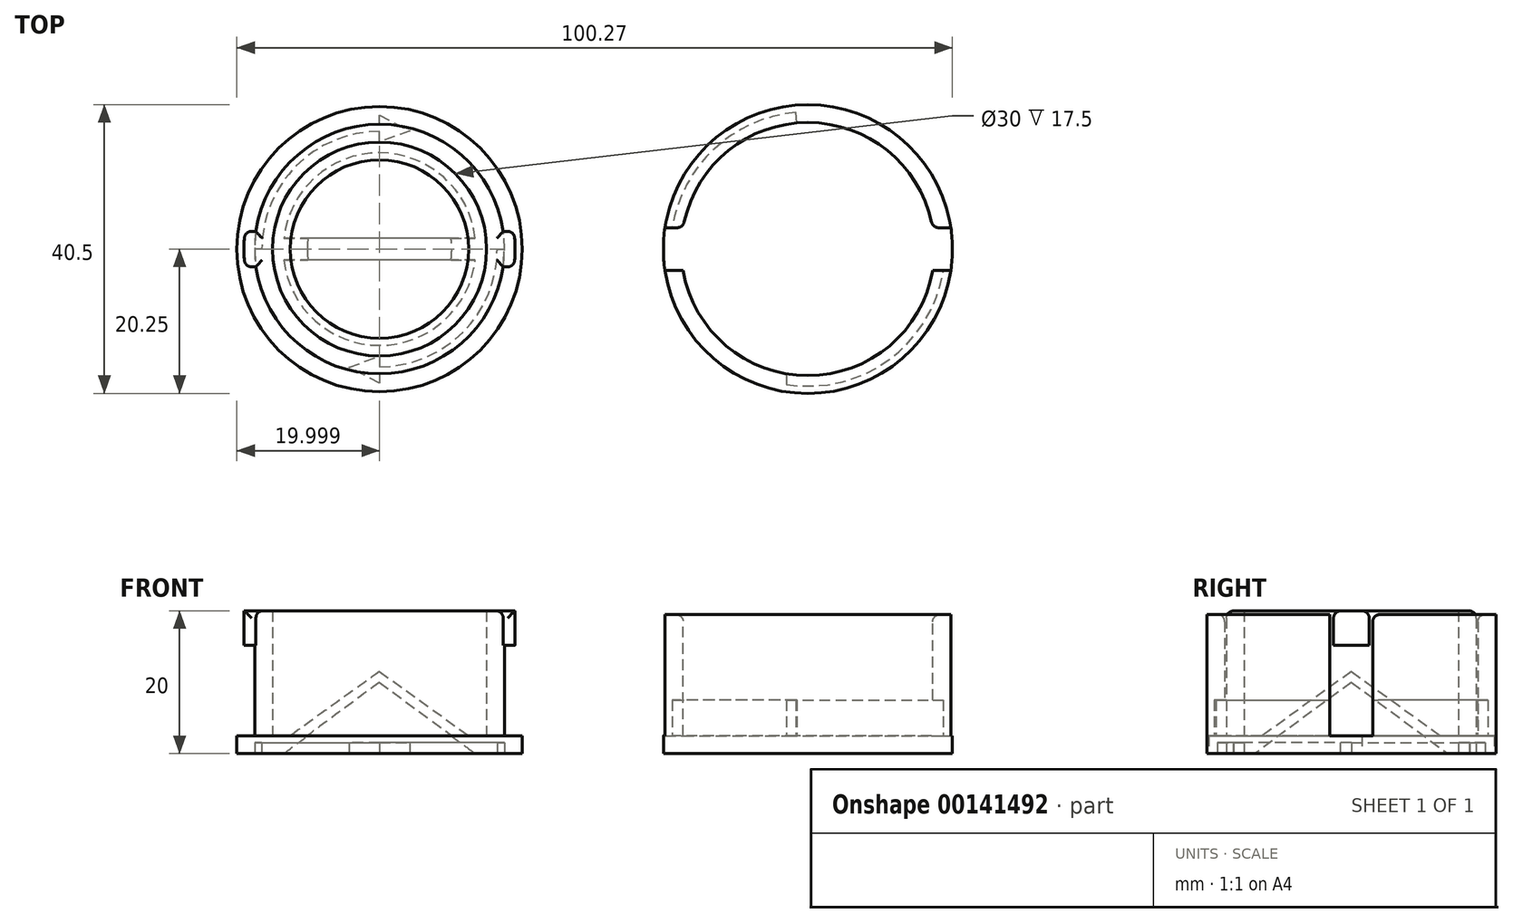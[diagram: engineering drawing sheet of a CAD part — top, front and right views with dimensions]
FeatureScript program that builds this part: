
annotation { "Feature Type Name" : "Feature", "Feature Type Description" : "" }
export const myFeature = defineFeature(function(context is Context, id is Id, definition is map)
    precondition{}
    {
        {
            var Q0;
            Q0=qCreatedBy(makeId("Top.planeOp"),FACE);
            var sketch = newSketch(context, id + "F0", { "sketchPlane" : qUnion([Q0])});
            skCircle(sketch, "E0", {"center": v(-83.34, 0) * mm, "radius": 20.25 * mm});
            skSolve(sketch);
        }
        {
            var Q0;
            Q0=makeQuery(id+"F0.imprint","IMPRINT",FACE,{"disambiguationData":[TD([[makeQuery(id+"F0.imprint","IMPRINT",EDGE,{"derivedFrom":sQuery(id+"F0.wireOp",EDGE,"E0")}),1.0]])]});
            extrude(context, id + "F1", {"entities" : qUnion([Q0]), "depth" : (22 - 2.5) * mm});
        }
        {
            var Q0;
            Q0=makeQuery(id+"F1.opExtrude","CAP_FACE",FACE,{"disambiguationData":[OSD([sQuery(id+"F0.wireOp",EDGE,"E0")])],"isStart":false});
            shell(context, id + "F2", {"entities" : qUnion([Q0]), "thickness" : 2.5 * mm});
        }
        {
            var Q0;
            Q0=makeQuery(id+"F1.opExtrude","CAP_FACE",FACE,{"disambiguationData":[OSD([sQuery(id+"F0.wireOp",EDGE,"E0")])],"isStart":false});
            var sketch = newSketch(context, id + "F3", { "sketchPlane" : qUnion([Q0])});
            skLineSegment(sketch, "E1.bottom", {"start": v(-105.34, -3) * mm, "end": v(-61.34, -3) * mm});
            skLineSegment(sketch, "E1.top", {"start": v(-105.34, 3) * mm, "end": v(-61.34, 3) * mm});
            skLineSegment(sketch, "E1.left", {"start": v(-105.34, -3) * mm, "end": v(-105.34, 3) * mm});
            skLineSegment(sketch, "E1.right", {"start": v(-61.34, -3) * mm, "end": v(-61.34, 3) * mm});
            skPoint(sketch, "E1.middle", {"position": v(-83.34, 0) * mm});
            skSolve(sketch);
        }
        {
            var Q0;
            {var subQ0=sQuery(id+"F3.wireOp",EDGE,"E1.bottom");var subQ1=sQuery(id+"F0.wireOp",EDGE,"E0");var subQ2=makeQuery(id+"F1.opExtrude","CAP_EDGE",EDGE,{"disambiguationData":[OSD([subQ1])],"isStart":false});var subQ3=makeQuery(id+"F3.imprint","INTERSECT",VERTEX,{"disambiguationData":[OD(1.0)],"derivedFrom":[subQ2,subQ0]});Q0=makeQuery(id+"F3.imprint","IMPRINT",FACE,{"disambiguationData":[TD([[makeQuery(id+"F3.imprint","IMPRINT",EDGE,{"disambiguationData":[TD([[subQ3,-1.0]])],"derivedFrom":subQ2}),1.0]])]});}
            var Q1;
            {var subQ0=sQuery(id+"F3.wireOp",EDGE,"E1.bottom");var subQ1=sQuery(id+"F0.wireOp",EDGE,"E0");var subQ2=makeQuery(id+"F1.opExtrude","CAP_EDGE",EDGE,{"disambiguationData":[OSD([subQ1])],"isStart":false});var subQ3=makeQuery(id+"F3.imprint","INTERSECT",VERTEX,{"disambiguationData":[OD(0.0)],"derivedFrom":[subQ2,subQ0]});Q1=makeQuery(id+"F3.imprint","IMPRINT",FACE,{"disambiguationData":[TD([[makeQuery(id+"F3.imprint","IMPRINT",EDGE,{"disambiguationData":[TD([[subQ3,1.0]])],"derivedFrom":subQ2}),1.0]])]});}
            extrude(context, id + "F4", {"entities" : qUnion([Q0, Q1]), "operationType" : NewBodyOperationType.REMOVE, "oppositeDirection" : true, "depth" : (19.5 - 2.5) * mm});
        }
        {
            var Q0;
            {var subQ0=sQuery(id+"F3.wireOp",EDGE,"E1.bottom");var subQ1=sQuery(id+"F0.wireOp",EDGE,"E0");var subQ2=makeQuery(id+"F1.opExtrude","CAP_EDGE",EDGE,{"disambiguationData":[OSD([subQ1])],"isStart":false});var subQ3=makeQuery(id+"F2.opShell","OFFSET_EDGE",EDGE,{"disambiguationData":[OSD([subQ1]),TDD([subQ2])]});var subQ4=makeQuery(id+"F3.imprint","INTERSECT",VERTEX,{"disambiguationData":[OD(1.0)],"derivedFrom":[subQ3,subQ0]});var subQ5=sQuery(id+"F3.wireOp",EDGE,"E1.top");var subQ7=makeQuery(id+"F3.imprint","INTERSECT",VERTEX,{"disambiguationData":[OD(1.0)],"derivedFrom":[subQ2,subQ0]});var subQ8=makeQuery(id+"F3.imprint","INTERSECT",VERTEX,{"disambiguationData":[OD(1.0)],"derivedFrom":[subQ2,subQ5]});var subQ9=makeQuery(id+"F3.imprint","INTERSECT",VERTEX,{"disambiguationData":[OD(0.0)],"derivedFrom":[subQ3,subQ0]});var subQ11=makeQuery(id+"F3.imprint","INTERSECT",VERTEX,{"disambiguationData":[OD(0.0)],"derivedFrom":[subQ2,subQ0]});var subQ12=makeQuery(id+"F3.imprint","INTERSECT",VERTEX,{"disambiguationData":[OD(0.0)],"derivedFrom":[subQ2,subQ5]});Q0=makeQuery(id+"F4.boolean.opBoolean","MERGE",FACE,{"derivedFrom":[makeQuery(id+"F2.opShell","OFFSET_FACE",FACE,{"disambiguationData":[OSD([subQ1]),TDD([makeQuery(id+"F1.opExtrude","CAP_FACE",FACE,{"disambiguationData":[OSD([subQ1])],"isStart":true})])]}),makeQuery(id+"F4.opExtrude","CAP_FACE",FACE,{"disambiguationData":[OSD([subQ1,subQ0,subQ5]),TDD([makeQuery(id+"F3.imprint","IMPRINT",EDGE,{"disambiguationData":[TD([[subQ11,-1.0]])],"derivedFrom":subQ0}),makeQuery(id+"F3.imprint","IMPRINT",EDGE,{"disambiguationData":[TD([[subQ12,-1.0]])],"derivedFrom":subQ5}),makeQuery(id+"F3.imprint","IMPRINT",EDGE,{"disambiguationData":[TD([[subQ11,1.0]])],"derivedFrom":subQ2}),makeQuery(id+"F3.imprint","IMPRINT",EDGE,{"disambiguationData":[TD([[subQ9,1.0]])],"derivedFrom":subQ3})])],"isStart":false}),makeQuery(id+"F4.opExtrude","CAP_FACE",FACE,{"disambiguationData":[OSD([subQ1,subQ0,subQ5]),TDD([makeQuery(id+"F3.imprint","IMPRINT",EDGE,{"disambiguationData":[TD([[subQ7,1.0]])],"derivedFrom":subQ0}),makeQuery(id+"F3.imprint","IMPRINT",EDGE,{"disambiguationData":[TD([[subQ8,1.0]])],"derivedFrom":subQ5}),makeQuery(id+"F3.imprint","IMPRINT",EDGE,{"disambiguationData":[TD([[subQ7,-1.0]])],"derivedFrom":subQ2}),makeQuery(id+"F3.imprint","IMPRINT",EDGE,{"disambiguationData":[TD([[subQ4,-1.0]])],"derivedFrom":subQ3})])],"isStart":false})]});}
            var sketch = newSketch(context, id + "F5", { "sketchPlane" : qUnion([Q0])});
            skLineSegment(sketch, "E2.0.1", {"start": v(-102.33, 3) * mm, "end": v(-100.83, 3) * mm});
            skArc(sketch, "E2.0.2", {"start": v(-100.83, 3) * mm, "mid": v(-95.37, 13.05) * mm, "end": v(-84.9, 17.68) * mm});
            skLineSegment(sketch, "E3.0.2", {"start": v(-64.34, -3) * mm, "end": v(-65.84, -3) * mm});
            skArc(sketch, "E3.0.3", {"start": v(-65.84, -3) * mm, "mid": v(-73.09, -14.5) * mm, "end": v(-86.34, -17.5) * mm});
            skLineSegment(sketch, "E4", {"start": v(-86.34, -17.5) * mm, "end": v(-86.34, -19) * mm});
            skPoint(sketch, "E4.endSnap0", {"position": v(-86.34, -20.16) * mm});
            skPoint(sketch, "E2.0.3.end.orphan", {"position": v(-63.3, 3) * mm});
            skPoint(sketch, "E2.0.3.start.orphan", {"position": v(-65.84, 3) * mm});
            skPoint(sketch, "E3.0.0.end.orphan", {"position": v(-103.36, -3) * mm});
            skPoint(sketch, "E3.0.0.start.orphan", {"position": v(-100.83, -3) * mm});
            skPoint(sketch, "E5.orphan", {"position": v(-86.34, -22.28) * mm});
            skArc(sketch, "E6.0", {"start": v(-86.34, -19) * mm, "mid": v(-72.03, -15.55) * mm, "end": v(-64.34, -3) * mm});
            skArc(sketch, "E7.0", {"start": v(-85.03, 19.16) * mm, "mid": v(-96.46, 14.05) * mm, "end": v(-102.33, 3) * mm});
            skPoint(sketch, "E8.orphan", {"position": v(-63.3, -3) * mm});
            skPoint(sketch, "E2.0.0.end.orphan", {"position": v(-103.36, 3) * mm});
            skLineSegment(sketch, "E9", {"start": v(-84.9, 17.68) * mm, "end": v(-85.03, 19.16) * mm});
            skSolve(sketch);
        }
        {
            var Q0;
            Q0 = qSketchRegion(id + "F5", true);
            extrude(context, id + "F6", {"entities" : qUnion([Q0]), "depth" : 5 * mm});
        }
        {
            var Q0;
            Q0=makeQuery(id+"F6.opExtrude","SWEPT_BODY",BODY,{"disambiguationData":[OSD([sQuery(id+"F5.wireOp",EDGE,"E2.0.0"),sQuery(id+"F5.wireOp",EDGE,"E2.0.1"),sQuery(id+"F5.wireOp",EDGE,"E2.0.2"),sQuery(id+"F5.wireOp",EDGE,"b0c8b627-6731-4ba6-8ec9-004736f8713d.trimOffspring")])]});
            var Q1;
            Q1=makeQuery(id+"F6.opExtrude","SWEPT_BODY",BODY,{"disambiguationData":[OSD([sQuery(id+"F5.wireOp",EDGE,"E3.0.1"),sQuery(id+"F5.wireOp",EDGE,"E3.0.2"),sQuery(id+"F5.wireOp",EDGE,"E3.0.3"),sQuery(id+"F5.wireOp",EDGE,"E4")])]});
            var Q2;
            Q2=makeQuery(id+"F1.opExtrude","SWEPT_BODY",BODY,{"disambiguationData":[OSD([sQuery(id+"F0.wireOp",EDGE,"E0")])]});
            booleanBodies(context, id + "F7", {"operationType" : BooleanOperationType.SUBTRACTION, "tools" : qUnion([Q0, Q1]), "targets" : qUnion([Q2])});
        }
        {
            var Q0;
            {var subQ0=sQuery(id+"F3.wireOp",EDGE,"E1.bottom");var subQ1=sQuery(id+"F0.wireOp",EDGE,"E0");var subQ2=makeQuery(id+"F1.opExtrude","CAP_EDGE",EDGE,{"disambiguationData":[OSD([subQ1])],"isStart":false});Q0=makeQuery(id+"F4.boolean.opBoolean","COPY",EDGE,{"derivedFrom":makeQuery(id+"F4.opExtrude","CAP_EDGE",EDGE,{"disambiguationData":[OSD([subQ0]),TDD([makeQuery(id+"F3.imprint","IMPRINT",EDGE,{"disambiguationData":[TD([[makeQuery(id+"F3.imprint","INTERSECT",VERTEX,{"disambiguationData":[OD(1.0)],"derivedFrom":[subQ2,subQ0]}),1.0]])],"derivedFrom":subQ0})])],"isStart":true})});}
            var Q1;
            {var subQ0=sQuery(id+"F3.wireOp",EDGE,"E1.top");var subQ1=sQuery(id+"F0.wireOp",EDGE,"E0");var subQ2=makeQuery(id+"F1.opExtrude","CAP_EDGE",EDGE,{"disambiguationData":[OSD([subQ1])],"isStart":false});Q1=makeQuery(id+"F4.boolean.opBoolean","COPY",EDGE,{"derivedFrom":makeQuery(id+"F4.opExtrude","CAP_EDGE",EDGE,{"disambiguationData":[OSD([subQ0]),TDD([makeQuery(id+"F3.imprint","IMPRINT",EDGE,{"disambiguationData":[TD([[makeQuery(id+"F3.imprint","INTERSECT",VERTEX,{"disambiguationData":[OD(1.0)],"derivedFrom":[subQ2,subQ0]}),1.0]])],"derivedFrom":subQ0})])],"isStart":true})});}
            var Q2;
            {var subQ0=sQuery(id+"F3.wireOp",EDGE,"E1.top");var subQ1=sQuery(id+"F0.wireOp",EDGE,"E0");var subQ2=makeQuery(id+"F1.opExtrude","CAP_EDGE",EDGE,{"disambiguationData":[OSD([subQ1])],"isStart":false});Q2=makeQuery(id+"F4.boolean.opBoolean","COPY",EDGE,{"derivedFrom":makeQuery(id+"F4.opExtrude","CAP_EDGE",EDGE,{"disambiguationData":[OSD([subQ0]),TDD([makeQuery(id+"F3.imprint","IMPRINT",EDGE,{"disambiguationData":[TD([[makeQuery(id+"F3.imprint","INTERSECT",VERTEX,{"disambiguationData":[OD(0.0)],"derivedFrom":[subQ2,subQ0]}),-1.0]])],"derivedFrom":subQ0})])],"isStart":true})});}
            var Q3;
            {var subQ0=sQuery(id+"F3.wireOp",EDGE,"E1.bottom");var subQ1=sQuery(id+"F0.wireOp",EDGE,"E0");var subQ2=makeQuery(id+"F1.opExtrude","CAP_EDGE",EDGE,{"disambiguationData":[OSD([subQ1])],"isStart":false});Q3=makeQuery(id+"F4.boolean.opBoolean","COPY",EDGE,{"derivedFrom":makeQuery(id+"F4.opExtrude","CAP_EDGE",EDGE,{"disambiguationData":[OSD([subQ0]),TDD([makeQuery(id+"F3.imprint","IMPRINT",EDGE,{"disambiguationData":[TD([[makeQuery(id+"F3.imprint","INTERSECT",VERTEX,{"disambiguationData":[OD(0.0)],"derivedFrom":[subQ2,subQ0]}),-1.0]])],"derivedFrom":subQ0})])],"isStart":true})});}
            var Q4;
            Q4=makeQuery(id+"F7.opBoolean","COPY",EDGE,{"derivedFrom":makeQuery(id+"F6.opExtrude","SWEPT_EDGE",EDGE,{"disambiguationData":[OSD([sQuery(id+"F3.wireOp",EDGE,"E1.bottom"),sQuery(id+"F5.wireOp",EDGE,"E3.0.2"),sQuery(id+"F5.wireOp",EDGE,"E6.0")])]})});
            var Q5;
            Q5=makeQuery(id+"F7.opBoolean","COPY",EDGE,{"derivedFrom":makeQuery(id+"F6.opExtrude","SWEPT_EDGE",EDGE,{"disambiguationData":[OSD([sQuery(id+"F3.wireOp",EDGE,"E1.top"),sQuery(id+"F5.wireOp",EDGE,"E2.0.1"),sQuery(id+"F5.wireOp",EDGE,"E7.0")])]})});
            fillet(context, id + "F8", {"entities" : qUnion([Q0, Q1, Q2, Q3, Q4, Q5]), "radius" : 1 * mm, "tangentPropagation" : true, "allowEdgeOverflow" : false});
        }
        {
            var Q0;
            {var subQ0=sQuery(id+"F0.wireOp",EDGE,"E0");var subQ1=sQuery(id+"F3.wireOp",EDGE,"E1.top");var subQ2=makeQuery(id+"F1.opExtrude","CAP_EDGE",EDGE,{"disambiguationData":[OSD([subQ0])],"isStart":false});var subQ3=makeQuery(id+"F2.opShell","OFFSET_EDGE",EDGE,{"disambiguationData":[OSD([subQ0]),TDD([subQ2])]});Q0=makeQuery(id+"F4.boolean.opBoolean","SPLIT",EDGE,{"disambiguationData":[TD([makeQuery(id+"F4.opExtrude","SWEPT_FACE",FACE,{"disambiguationData":[OSD([subQ1]),TDD([makeQuery(id+"F3.imprint","IMPRINT",EDGE,{"disambiguationData":[TD([[makeQuery(id+"F3.imprint","INTERSECT",VERTEX,{"disambiguationData":[OD(0.0)],"derivedFrom":[subQ2,subQ1]}),-1.0]])],"derivedFrom":subQ1})])]})])],"derivedFrom":subQ3});}
            var Q1;
            {var subQ0=sQuery(id+"F0.wireOp",EDGE,"E0");var subQ1=sQuery(id+"F3.wireOp",EDGE,"E1.bottom");var subQ2=makeQuery(id+"F1.opExtrude","CAP_EDGE",EDGE,{"disambiguationData":[OSD([subQ0])],"isStart":false});var subQ3=makeQuery(id+"F2.opShell","OFFSET_EDGE",EDGE,{"disambiguationData":[OSD([subQ0]),TDD([subQ2])]});Q1=makeQuery(id+"F4.boolean.opBoolean","SPLIT",EDGE,{"disambiguationData":[TD([makeQuery(id+"F4.opExtrude","SWEPT_FACE",FACE,{"disambiguationData":[OSD([subQ1]),TDD([makeQuery(id+"F3.imprint","IMPRINT",EDGE,{"disambiguationData":[TD([[makeQuery(id+"F3.imprint","INTERSECT",VERTEX,{"disambiguationData":[OD(0.0)],"derivedFrom":[subQ2,subQ1]}),-1.0]])],"derivedFrom":subQ1})])]})])],"derivedFrom":subQ3});}
            fillet(context, id + "F9", {"entities" : qUnion([Q0, Q1]), "radius" : 1 * mm, "tangentPropagation" : true, "allowEdgeOverflow" : false});
        }
        {
            var Q0;
            Q0=qCreatedBy(makeId("Front.planeOp"),FACE);
            var sketch = newSketch(context, id + "F10", { "sketchPlane" : qUnion([Q0])});
            skLineSegment(sketch, "E10", {"start": v(-123.36, 0) * mm, "end": v(-163.36, 0) * mm, "construction": true});
            skLineSegment(sketch, "E11", {"start": v(-123.36, 0) * mm, "end": v(-129.86, 0) * mm});
            skLineSegment(sketch, "E12", {"start": v(-129.86, 0) * mm, "end": v(-143.36, 10) * mm});
            skPoint(sketch, "E12.endSnap0", {"position": v(-143.36, 0) * mm});
            skLineSegment(sketch, "E13", {"start": v(-143.36, 10) * mm, "end": v(-143.36, 11.5) * mm});
            skLineSegment(sketch, "E14", {"start": v(-143.36, 11.5) * mm, "end": v(-130.86, 2.5) * mm});
            skLineSegment(sketch, "E15", {"start": v(-130.86, 2.5) * mm, "end": v(-128.36, 2.5) * mm});
            skLineSegment(sketch, "E16", {"start": v(-128.36, 2.5) * mm, "end": v(-128.36, 20) * mm});
            skLineSegment(sketch, "E17", {"start": v(-128.36, 20) * mm, "end": v(-125.86, 20) * mm});
            skLineSegment(sketch, "E18", {"start": v(-125.86, 20) * mm, "end": v(-125.86, 2.5) * mm});
            skLineSegment(sketch, "E19", {"start": v(-125.86, 2.5) * mm, "end": v(-123.36, 2.5) * mm});
            skLineSegment(sketch, "E20", {"start": v(-123.36, 2.5) * mm, "end": v(-123.36, 0) * mm});
            skSolve(sketch);
        }
        {
            var Q0;
            Q0=makeQuery(id+"F10.imprint","IMPRINT",FACE,{"disambiguationData":[TD([[makeQuery(id+"F10.imprint","IMPRINT",EDGE,{"derivedFrom":sQuery(id+"F10.wireOp",EDGE,"E11")}),-1.0]])]});
            var Q1;
            Q1=sQuery(id+"F10.wireOp",EDGE,"E13");
            revolve(context, id + "F11", {"entities" : qUnion([Q0]), "axis" : qUnion([Q1]), "revolveType" : RevolveType.FULL});
        }
        {
            var Q0;
            Q0=makeQuery(id+"F11.opRevolve","SWEPT_FACE",FACE,{"disambiguationData":[OSD([sQuery(id+"F10.wireOp",EDGE,"E11")])]});
            var sketch = newSketch(context, id + "F12", { "sketchPlane" : qUnion([Q0])});
            skCircle(sketch, "E21.0", {"center": v(-143.36, 0) * mm, "radius": 17.5 * mm, "construction": true});
            skCircle(sketch, "E22.0", {"center": v(-143.4, 0.19) * mm, "radius": 16.7 * mm, "construction": true});
            skLineSegment(sketch, "E23.bottom", {"start": v(-126.8, -1.5) * mm, "end": v(-159.93, -1.5) * mm});
            skLineSegment(sketch, "E23.top", {"start": v(-126.8, 1.5) * mm, "end": v(-159.93, 1.5) * mm});
            skLineSegment(sketch, "E23.left", {"start": v(-126.8, -1.5) * mm, "end": v(-126.8, 1.5) * mm});
            skLineSegment(sketch, "E23.right", {"start": v(-159.93, -1.5) * mm, "end": v(-159.93, 1.5) * mm});
            skSolve(sketch);
        }
        {
            var Q0;
            {var subQ0=sQuery(id+"F12.wireOp",EDGE,"E23.bottom");var subQ1=makeQuery(id+"F11.opRevolve","SWEPT_EDGE",EDGE,{"disambiguationData":[OSD([sQuery(id+"F10.wireOp",EDGE,"E11"),sQuery(id+"F10.wireOp",EDGE,"E12")])]});var subQ2=makeQuery(id+"F12.imprint","INTERSECT",VERTEX,{"disambiguationData":[OD(0.0)],"derivedFrom":[subQ1,subQ0]});Q0=makeQuery(id+"F12.imprint","IMPRINT",FACE,{"disambiguationData":[TD([[makeQuery(id+"F12.imprint","IMPRINT",EDGE,{"disambiguationData":[TD([[subQ2,-1.0]])],"derivedFrom":subQ0}),-1.0]])]});}
            extrude(context, id + "F13", {"entities" : qUnion([Q0]), "operationType" : NewBodyOperationType.ADD, "oppositeDirection" : true, "depth" : 2.5 * mm});
        }
        {
            var Q0;
            Q0=makeQuery(id+"F11.opRevolve","SWEPT_FACE",FACE,{"disambiguationData":[OSD([sQuery(id+"F10.wireOp",EDGE,"E17")])]});
            var sketch = newSketch(context, id + "F14", { "sketchPlane" : qUnion([Q0])});
            skCircle(sketch, "E24.0", {"center": v(-143.36, 0) * mm, "radius": 17.5 * mm});
            skLineSegment(sketch, "E25.bottom", {"start": v(-162.2, 2.5) * mm, "end": v(-160.68, 2.5) * mm});
            skLineSegment(sketch, "E25.top", {"start": v(-162.2, -2.5) * mm, "end": v(-160.68, -2.5) * mm});
            skArc(sketch, "E26.0", {"start": v(-124.53, -2.5) * mm, "mid": v(-124.36, 0) * mm, "end": v(-124.53, 2.5) * mm});
            skPoint(sketch, "E25.left.end.orphan", {"position": v(-165.72, -2.5) * mm});
            skPoint(sketch, "E27.orphan", {"position": v(-165.72, 2.5) * mm});
            skArc(sketch, "E28.trimOffspring", {"start": v(-162.2, 2.5) * mm, "mid": v(-162.36, 0) * mm, "end": v(-162.2, -2.5) * mm});
            skLineSegment(sketch, "E29.trimOffspring", {"start": v(-126.04, 2.5) * mm, "end": v(-124.53, 2.5) * mm});
            skLineSegment(sketch, "E30.trimOffspring", {"start": v(-126.04, -2.5) * mm, "end": v(-124.53, -2.5) * mm});
            skPoint(sketch, "E25.right.start.orphan", {"position": v(-121, 2.5) * mm});
            skPoint(sketch, "E31.orphan", {"position": v(-121, -2.5) * mm});
            skSolve(sketch);
        }
        {
            var Q0;
            Q0=makeQuery(id+"F14.imprint","IMPRINT",FACE,{"disambiguationData":[TD([[makeQuery(id+"F14.imprint","IMPRINT",EDGE,{"derivedFrom":sQuery(id+"F14.wireOp",EDGE,"E26.0")}),1.0]])]});
            var Q1;
            {var subQ0=sQuery(id+"F14.wireOp",EDGE,"E25.bottom");Q1=makeQuery(id+"F14.imprint","IMPRINT",FACE,{"disambiguationData":[TD([[makeQuery(id+"F14.imprint","IMPRINT",EDGE,{"derivedFrom":subQ0}),-1.0]])]});}
            extrude(context, id + "F15", {"entities" : qUnion([Q0, Q1]), "operationType" : NewBodyOperationType.ADD, "oppositeDirection" : true, "depth" : 4.8 * mm});
        }
        {
            var Q0;
            {var subQ0=sQuery(id+"F14.wireOp",EDGE,"E25.bottom");var subQ3=sQuery(id+"F10.wireOp",EDGE,"E18");var subQ4=sQuery(id+"F10.wireOp",EDGE,"E17");Q0=makeQuery(id+"F15.boolean.opBoolean","SPLIT",EDGE,{"disambiguationData":[TD([makeQuery(id+"F15.opExtrude","SWEPT_FACE",FACE,{"disambiguationData":[OSD([subQ0])]})])],"derivedFrom":makeQuery(id+"F11.opRevolve","SWEPT_EDGE",EDGE,{"disambiguationData":[OSD([subQ4,subQ3])]})});}
            var Q1;
            {var subQ0=sQuery(id+"F14.wireOp",EDGE,"E25.top");var subQ3=sQuery(id+"F10.wireOp",EDGE,"E18");var subQ4=sQuery(id+"F10.wireOp",EDGE,"E17");Q1=makeQuery(id+"F15.boolean.opBoolean","SPLIT",EDGE,{"disambiguationData":[TD([makeQuery(id+"F15.opExtrude","SWEPT_FACE",FACE,{"disambiguationData":[OSD([subQ0])]})])],"derivedFrom":makeQuery(id+"F11.opRevolve","SWEPT_EDGE",EDGE,{"disambiguationData":[OSD([subQ4,subQ3])]})});}
            var Q2;
            Q2=makeQuery(id+"F15.opExtrude","CAP_EDGE",EDGE,{"disambiguationData":[OSD([sQuery(id+"F14.wireOp",EDGE,"E29.trimOffspring")])],"isStart":true});
            var Q3;
            Q3=makeQuery(id+"F15.opExtrude","CAP_EDGE",EDGE,{"disambiguationData":[OSD([sQuery(id+"F14.wireOp",EDGE,"E30.trimOffspring")])],"isStart":true});
            var Q4;
            Q4=makeQuery(id+"F15.opExtrude","CAP_EDGE",EDGE,{"disambiguationData":[OSD([sQuery(id+"F14.wireOp",EDGE,"E25.bottom")])],"isStart":true});
            var Q5;
            Q5=makeQuery(id+"F15.opExtrude","CAP_EDGE",EDGE,{"disambiguationData":[OSD([sQuery(id+"F14.wireOp",EDGE,"E25.top")])],"isStart":true});
            var Q6;
            Q6=makeQuery(id+"F15.opExtrude","SWEPT_EDGE",EDGE,{"disambiguationData":[OSD([sQuery(id+"F14.wireOp",EDGE,"E25.bottom"),sQuery(id+"F14.wireOp",EDGE,"E28.trimOffspring")])]});
            var Q7;
            Q7=makeQuery(id+"F15.opExtrude","SWEPT_EDGE",EDGE,{"disambiguationData":[OSD([sQuery(id+"F14.wireOp",EDGE,"E25.top"),sQuery(id+"F14.wireOp",EDGE,"E28.trimOffspring")])]});
            var Q8;
            Q8=makeQuery(id+"F15.opExtrude","SWEPT_EDGE",EDGE,{"disambiguationData":[OSD([sQuery(id+"F14.wireOp",EDGE,"E26.0"),sQuery(id+"F14.wireOp",EDGE,"E30.trimOffspring")])]});
            var Q9;
            Q9=makeQuery(id+"F15.opExtrude","SWEPT_EDGE",EDGE,{"disambiguationData":[OSD([sQuery(id+"F14.wireOp",EDGE,"E26.0"),sQuery(id+"F14.wireOp",EDGE,"E29.trimOffspring")])]});
            fillet(context, id + "F16", {"entities" : qUnion([Q0, Q1, Q2, Q3, Q4, Q5, Q6, Q7, Q8, Q9]), "radius" : 1 * mm, "tangentPropagation" : true, "allowEdgeOverflow" : false});
        }
        {
            var Q0;
            {var subQ0=sQuery(id+"F10.wireOp",EDGE,"E11");Q0=makeQuery(id+"F13.boolean.opBoolean","MERGE",FACE,{"derivedFrom":[makeQuery(id+"F11.opRevolve","SWEPT_FACE",FACE,{"disambiguationData":[OSD([subQ0])]}),makeQuery(id+"F13.opExtrude","CAP_FACE",FACE,{"disambiguationData":[OSD([subQ0,sQuery(id+"F10.wireOp",EDGE,"E12"),sQuery(id+"F12.wireOp",EDGE,"E23.bottom"),sQuery(id+"F12.wireOp",EDGE,"E23.top")])],"isStart":true})]});}
            var sketch = newSketch(context, id + "F17", { "sketchPlane" : qUnion([Q0])});
            skCircle(sketch, "E32.0", {"center": v(-143.36, 0) * mm, "radius": 20 * mm});
            skArc(sketch, "E33.0", {"start": v(-160.86, 0) * mm, "mid": v(-155.74, -12.37) * mm, "end": v(-143.36, -17.5) * mm});
            skArc(sketch, "E34.0", {"start": v(-159.86, 0) * mm, "mid": v(-155.03, -11.67) * mm, "end": v(-143.36, -16.5) * mm});
            skLineSegment(sketch, "E35", {"start": v(-159.86, 0) * mm, "end": v(-160.86, 0) * mm});
            skLineSegment(sketch, "E36", {"start": v(-143.36, -17.5) * mm, "end": v(-143.36, -18.78) * mm});
            skLineSegment(sketch, "E37", {"start": v(-143.36, -18.78) * mm, "end": v(-139.13, -16.58) * mm});
            skLineSegment(sketch, "E38", {"start": v(-139.13, -16.58) * mm, "end": v(-143.36, -15.03) * mm});
            skLineSegment(sketch, "E39", {"start": v(-143.36, -15.03) * mm, "end": v(-143.36, -16.5) * mm});
            skSolve(sketch);
        }
        {
            var Q0;
            Q0=makeQuery(id+"F17.imprint","IMPRINT",FACE,{"disambiguationData":[TD([[makeQuery(id+"F17.imprint","IMPRINT",EDGE,{"derivedFrom":sQuery(id+"F17.wireOp",EDGE,"E33.0")}),1.0]])]});
            extrude(context, id + "F18", {"entities" : qUnion([Q0]), "oppositeDirection" : true, "depth" : 1.5 * mm});
        }
        {
            var Q0;
            Q0=makeQuery(id+"F18.opExtrude","SWEPT_BODY",BODY,{"disambiguationData":[OSD([sQuery(id+"F17.wireOp",EDGE,"E33.0"),sQuery(id+"F17.wireOp",EDGE,"E34.0"),sQuery(id+"F17.wireOp",EDGE,"E35"),sQuery(id+"F17.wireOp",EDGE,"E36"),sQuery(id+"F17.wireOp",EDGE,"E37"),sQuery(id+"F17.wireOp",EDGE,"E38"),sQuery(id+"F17.wireOp",EDGE,"E39")])]});
            var Q1;
            Q1=makeQuery(id+"F11.opRevolve","SWEPT_EDGE",EDGE,{"disambiguationData":[OSD([sQuery(id+"F10.wireOp",EDGE,"E11"),sQuery(id+"F10.wireOp",EDGE,"E20")])]});
            circularPattern(context, id + "F19", {"entities" : qUnion([Q0]), "axis" : qUnion([Q1]), "angle" : 180 * degree, "instanceCount" : 2});
        }
        {
            var Q0;
            Q0=makeQuery(id+"F19.opPattern","COPY",BODY,{"derivedFrom":makeQuery(id+"F18.opExtrude","SWEPT_BODY",BODY,{"disambiguationData":[OSD([sQuery(id+"F17.wireOp",EDGE,"E33.0"),sQuery(id+"F17.wireOp",EDGE,"E34.0"),sQuery(id+"F17.wireOp",EDGE,"E35"),sQuery(id+"F17.wireOp",EDGE,"E36"),sQuery(id+"F17.wireOp",EDGE,"E37"),sQuery(id+"F17.wireOp",EDGE,"E38"),sQuery(id+"F17.wireOp",EDGE,"E39")])]}),"instanceName":"1"});
            var Q1;
            Q1=makeQuery(id+"F18.opExtrude","SWEPT_BODY",BODY,{"disambiguationData":[OSD([sQuery(id+"F17.wireOp",EDGE,"E33.0"),sQuery(id+"F17.wireOp",EDGE,"E34.0"),sQuery(id+"F17.wireOp",EDGE,"E35"),sQuery(id+"F17.wireOp",EDGE,"E36"),sQuery(id+"F17.wireOp",EDGE,"E37"),sQuery(id+"F17.wireOp",EDGE,"E38"),sQuery(id+"F17.wireOp",EDGE,"E39")])]});
            var Q2;
            Q2=makeQuery(id+"F11.opRevolve","SWEPT_BODY",BODY,{"disambiguationData":[OSD([sQuery(id+"F10.wireOp",EDGE,"E11"),sQuery(id+"F10.wireOp",EDGE,"E12"),sQuery(id+"F10.wireOp",EDGE,"E13"),sQuery(id+"F10.wireOp",EDGE,"E14"),sQuery(id+"F10.wireOp",EDGE,"E15"),sQuery(id+"F10.wireOp",EDGE,"E16"),sQuery(id+"F10.wireOp",EDGE,"E17"),sQuery(id+"F10.wireOp",EDGE,"E18"),sQuery(id+"F10.wireOp",EDGE,"E19"),sQuery(id+"F10.wireOp",EDGE,"E20")])]});
            booleanBodies(context, id + "F20", {"operationType" : BooleanOperationType.SUBTRACTION, "tools" : qUnion([Q0, Q1]), "targets" : qUnion([Q2])});
        }
    });
